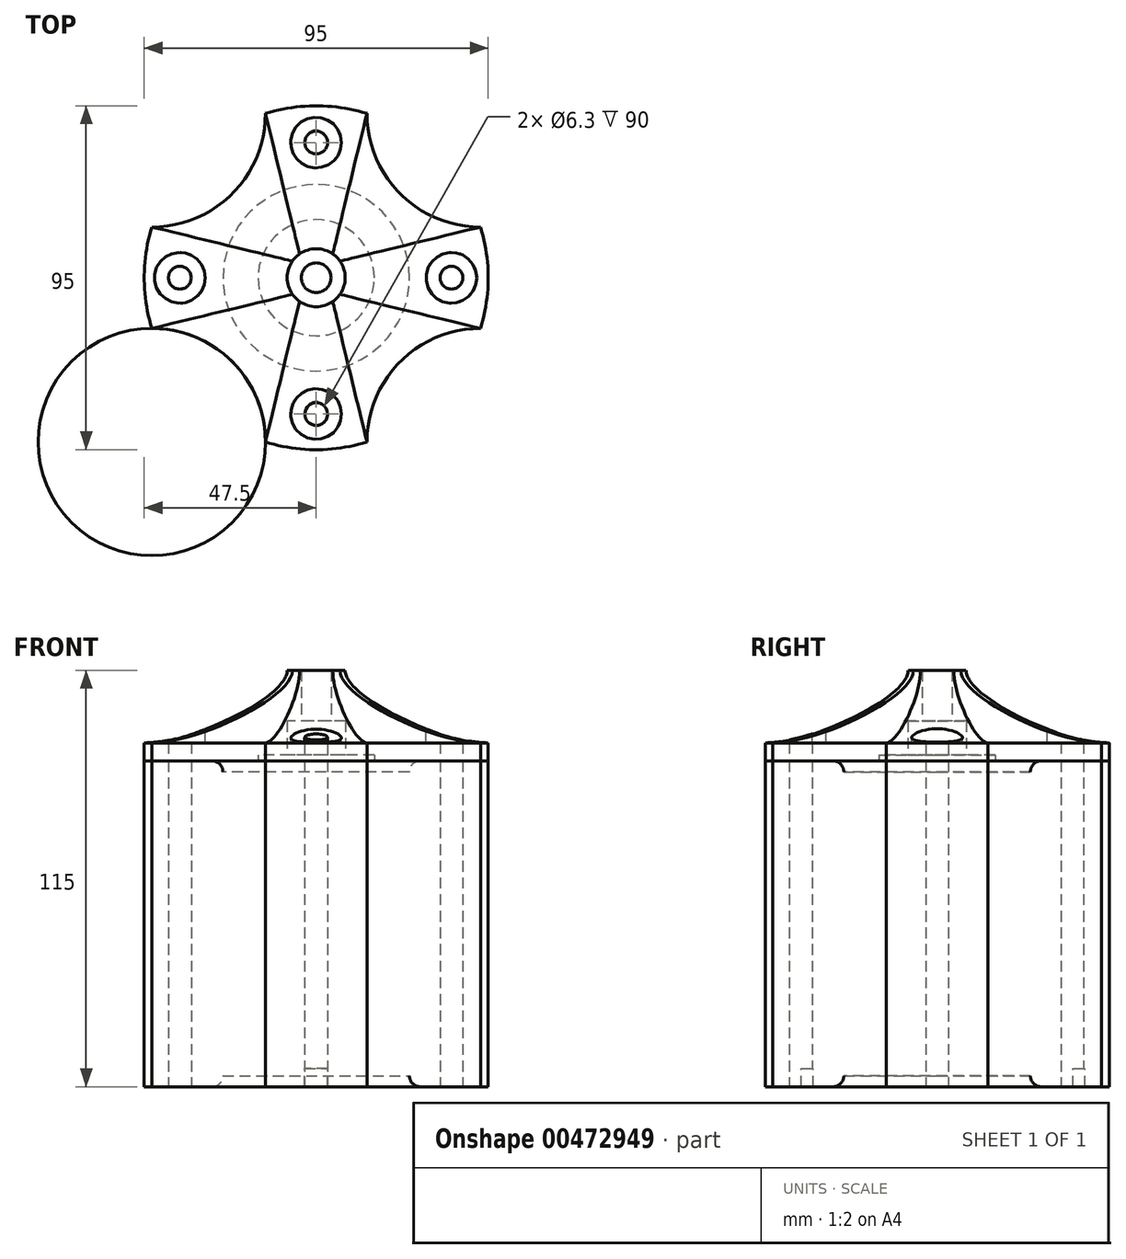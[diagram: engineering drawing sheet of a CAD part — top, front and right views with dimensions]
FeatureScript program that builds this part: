
annotation { "Feature Type Name" : "Feature", "Feature Type Description" : "" }
export const myFeature = defineFeature(function(context is Context, id is Id, definition is map)
    precondition{}
    {
        {
            var Q0;
            Q0=qCreatedBy(makeId("Top.planeOp"),FACE);
            var sketch = newSketch(context, id + "F0", { "sketchPlane" : qUnion([Q0])});
            skArc(sketch, "E0", {"start": v(14, 45.39) * mm, "mid": v(0, 47.5) * mm, "end": v(-14, 45.39) * mm});
            skLineSegment(sketch, "E1", {"start": v(0, 0) * mm, "end": v(47.5, 0) * mm, "construction": true});
            skLineSegment(sketch, "E2", {"start": v(0, 0) * mm, "end": v(-47.5, 0) * mm, "construction": true});
            skLineSegment(sketch, "E3", {"start": v(0, 0) * mm, "end": v(0, 47.5) * mm, "construction": true});
            skLineSegment(sketch, "E4", {"start": v(0, 0) * mm, "end": v(0, -47.5) * mm});
            skCircle(sketch, "E5", {"center": v(37.35, 0) * mm, "radius": 3.15 * mm});
            skCircle(sketch, "E6", {"center": v(-37.65, 0) * mm, "radius": 3.15 * mm});
            skCircle(sketch, "E7", {"center": v(0, 37.35) * mm, "radius": 3.15 * mm});
            skCircle(sketch, "E8", {"center": v(0, -37.65) * mm, "radius": 3.15 * mm});
            skLineSegment(sketch, "E9", {"start": v(14, -45.39) * mm, "end": v(14, 45.39) * mm, "construction": true});
            skLineSegment(sketch, "E10", {"start": v(-14, -45.39) * mm, "end": v(-14, 45.39) * mm, "construction": true});
            skLineSegment(sketch, "E11", {"start": v(-45.39, 14) * mm, "end": v(-14, 14) * mm, "construction": true});
            skLineSegment(sketch, "E12", {"start": v(-45.39, -14) * mm, "end": v(-14, -14) * mm});
            skArc(sketch, "E13.trimOffspring", {"start": v(-45.39, 14) * mm, "mid": v(-47.5, 0) * mm, "end": v(-45.39, -14) * mm});
            skArc(sketch, "E14.trimOffspring", {"start": v(-14, -45.39) * mm, "mid": v(0, -47.5) * mm, "end": v(14, -45.39) * mm});
            skArc(sketch, "E15.trimOffspring", {"start": v(45.39, -14) * mm, "mid": v(47.5, 0) * mm, "end": v(45.39, 14) * mm});
            skArc(sketch, "E16", {"start": v(-45.39, 14) * mm, "mid": v(-23.2, 23.2) * mm, "end": v(-14, 45.39) * mm});
            skLineSegment(sketch, "E17.top", {"start": v(14, 14) * mm, "end": v(45.39, 14) * mm, "construction": true});
            skLineSegment(sketch, "E17.left", {"start": v(14, 45.39) * mm, "end": v(14, 14) * mm, "construction": true});
            skLineSegment(sketch, "E18.top", {"start": v(14, -14) * mm, "end": v(45.39, -14) * mm, "construction": true});
            skLineSegment(sketch, "E18.left", {"start": v(14, -45.39) * mm, "end": v(14, -14) * mm, "construction": true});
            skLineSegment(sketch, "E19.top", {"start": v(-14, -14) * mm, "end": v(-45.39, -14) * mm, "construction": true});
            skLineSegment(sketch, "E19.left", {"start": v(-14, -45.39) * mm, "end": v(-14, -14) * mm, "construction": true});
            skArc(sketch, "E20", {"start": v(-14, -45.39) * mm, "mid": v(-23.2, -23.2) * mm, "end": v(-45.39, -14) * mm});
            skArc(sketch, "E21", {"start": v(45.39, -14) * mm, "mid": v(23.2, -23.2) * mm, "end": v(14, -45.39) * mm});
            skArc(sketch, "E22", {"start": v(14, 45.39) * mm, "mid": v(23.2, 23.2) * mm, "end": v(45.39, 14) * mm});
            skLineSegment(sketch, "E23.trimOffspring", {"start": v(14, 14) * mm, "end": v(45.39, 14) * mm});
            skLineSegment(sketch, "E24.trimOffspring", {"start": v(14, -14) * mm, "end": v(45.39, -14) * mm});
            skCircle(sketch, "E25", {"center": v(0, 0) * mm, "radius": 25.75 * mm});
            skSolve(sketch);
        }
        {
            var Q0;
            Q0=makeQuery(id+"F0.imprint","IMPRINT",FACE,{"disambiguationData":[TD([[makeQuery(id+"F0.imprint","IMPRINT",EDGE,{"derivedFrom":sQuery(id+"F0.wireOp",EDGE,"E0")}),1.0]])]});
            var Q1;
            {var subQ0=sQuery(id+"F0.wireOp",EDGE,"E20");Q1=makeQuery(id+"F0.imprint","IMPRINT",FACE,{"disambiguationData":[TD([[makeQuery(id+"F0.imprint","IMPRINT",EDGE,{"derivedFrom":subQ0}),-1.0]])]});}
            var Q2;
            {var subQ3=sQuery(id+"F0.wireOp",EDGE,"E21");Q2=makeQuery(id+"F0.imprint","IMPRINT",FACE,{"disambiguationData":[TD([[makeQuery(id+"F0.imprint","IMPRINT",EDGE,{"derivedFrom":subQ3}),-1.0]])]});}
            var Q3;
            Q3=makeQuery(id+"F0.imprint","IMPRINT",FACE,{"disambiguationData":[TD([[makeQuery(id+"F0.imprint","IMPRINT",EDGE,{"derivedFrom":sQuery(id+"F0.wireOp",EDGE,"E5")}),-1.0]])]});
            var Q4;
            {var subQ0=sQuery(id+"F0.wireOp",EDGE,"E25");var subQ1=makeQuery(id+"F0.imprint","INTERSECT",VERTEX,{"derivedFrom":[sQuery(id+"F0.wireOp",EDGE,"E12"),subQ0]});Q4=makeQuery(id+"F0.imprint","IMPRINT",FACE,{"disambiguationData":[TD([[makeQuery(id+"F0.imprint","IMPRINT",EDGE,{"disambiguationData":[TD([[subQ1,1.0]])],"derivedFrom":subQ0}),1.0]])]});}
            extrude(context, id + "F1", {"entities" : qUnion([Q0, Q1, Q2, Q3, Q4]), "depth" : 80 * mm, "symmetric" : true});
        }
        {
            var Q0;
            Q0=makeQuery(id+"F1.opExtrude","CAP_FACE",FACE,{"disambiguationData":[OSD([sQuery(id+"F0.wireOp",EDGE,"E0"),sQuery(id+"F0.wireOp",EDGE,"E5"),sQuery(id+"F0.wireOp",EDGE,"E6"),sQuery(id+"F0.wireOp",EDGE,"E7"),sQuery(id+"F0.wireOp",EDGE,"E8"),sQuery(id+"F0.wireOp",EDGE,"E13.trimOffspring"),sQuery(id+"F0.wireOp",EDGE,"E14.trimOffspring"),sQuery(id+"F0.wireOp",EDGE,"E15.trimOffspring"),sQuery(id+"F0.wireOp",EDGE,"E16"),sQuery(id+"F0.wireOp",EDGE,"E20"),sQuery(id+"F0.wireOp",EDGE,"E21"),sQuery(id+"F0.wireOp",EDGE,"E22")])],"isStart":false});
            cPlane(context, id + "F2", {"entities" : qUnion([Q0]), "cplaneType" : CPlaneType.OFFSET, "offset" : 5 * mm, "width" : 150 * mm, "height" : 150 * mm});
        }
        {
            var Q0;
            Q0=qCreatedBy(id+"F2.planeOp",FACE);
            var sketch = newSketch(context, id + "F3", { "sketchPlane" : qUnion([Q0])});
            skArc(sketch, "E26", {"start": v(14, 45.39) * mm, "mid": v(0, 47.5) * mm, "end": v(-14, 45.39) * mm});
            skLineSegment(sketch, "E27", {"start": v(0, 0) * mm, "end": v(47.5, 0) * mm, "construction": true});
            skLineSegment(sketch, "E28", {"start": v(0, 0) * mm, "end": v(-47.5, 0) * mm, "construction": true});
            skLineSegment(sketch, "E29", {"start": v(0, 0) * mm, "end": v(0, 47.5) * mm, "construction": true});
            skLineSegment(sketch, "E30", {"start": v(0, 0) * mm, "end": v(0, -47.5) * mm});
            skCircle(sketch, "E31", {"center": v(37.35, 0) * mm, "radius": 3.15 * mm});
            skCircle(sketch, "E32", {"center": v(-37.65, 0) * mm, "radius": 3.15 * mm});
            skCircle(sketch, "E33", {"center": v(0, 37.35) * mm, "radius": 3.15 * mm});
            skCircle(sketch, "E34", {"center": v(0, -37.65) * mm, "radius": 3.15 * mm});
            skLineSegment(sketch, "E35", {"start": v(14, -45.39) * mm, "end": v(14, 45.39) * mm, "construction": true});
            skLineSegment(sketch, "E36", {"start": v(-14, -45.39) * mm, "end": v(-14, 45.39) * mm, "construction": true});
            skLineSegment(sketch, "E37", {"start": v(-45.39, 14) * mm, "end": v(-14, 14) * mm, "construction": true});
            skLineSegment(sketch, "E38", {"start": v(-45.39, -14) * mm, "end": v(-14, -14) * mm});
            skArc(sketch, "E39.trimOffspring", {"start": v(-45.39, 14) * mm, "mid": v(-47.5, 0) * mm, "end": v(-45.39, -14) * mm});
            skArc(sketch, "E40.trimOffspring", {"start": v(-14, -45.39) * mm, "mid": v(0, -47.5) * mm, "end": v(14, -45.39) * mm});
            skArc(sketch, "E41.trimOffspring", {"start": v(45.39, -14) * mm, "mid": v(47.5, 0) * mm, "end": v(45.39, 14) * mm});
            skArc(sketch, "E42", {"start": v(-45.39, 14) * mm, "mid": v(-23.2, 23.2) * mm, "end": v(-14, 45.39) * mm});
            skLineSegment(sketch, "E43.top", {"start": v(14, 14) * mm, "end": v(45.39, 14) * mm, "construction": true});
            skLineSegment(sketch, "E43.left", {"start": v(14, 45.39) * mm, "end": v(14, 14) * mm, "construction": true});
            skLineSegment(sketch, "E44.top", {"start": v(14, -14) * mm, "end": v(45.39, -14) * mm, "construction": true});
            skLineSegment(sketch, "E44.left", {"start": v(14, -45.39) * mm, "end": v(14, -14) * mm, "construction": true});
            skLineSegment(sketch, "E45.top", {"start": v(-14, -14) * mm, "end": v(-45.39, -14) * mm, "construction": true});
            skLineSegment(sketch, "E45.left", {"start": v(-14, -45.39) * mm, "end": v(-14, -14) * mm, "construction": true});
            skArc(sketch, "E46", {"start": v(-14, -45.39) * mm, "mid": v(-23.2, -23.2) * mm, "end": v(-45.39, -14) * mm});
            skArc(sketch, "E47", {"start": v(45.39, -14) * mm, "mid": v(23.2, -23.2) * mm, "end": v(14, -45.39) * mm});
            skArc(sketch, "E48", {"start": v(14, 45.39) * mm, "mid": v(23.2, 23.2) * mm, "end": v(45.39, 14) * mm});
            skLineSegment(sketch, "E49.trimOffspring", {"start": v(14, 14) * mm, "end": v(45.39, 14) * mm});
            skLineSegment(sketch, "E50.trimOffspring", {"start": v(14, -14) * mm, "end": v(45.39, -14) * mm});
            skCircle(sketch, "E51", {"center": v(0, 0) * mm, "radius": 25.75 * mm});
            skSolve(sketch);
        }
        {
            var Q0;
            Q0=makeQuery(id+"F3.imprint","IMPRINT",FACE,{"disambiguationData":[TD([[makeQuery(id+"F3.imprint","IMPRINT",EDGE,{"derivedFrom":sQuery(id+"F3.wireOp",EDGE,"E26")}),1.0]])]});
            var Q1;
            Q1=makeQuery(id+"F3.imprint","IMPRINT",FACE,{"disambiguationData":[TD([[makeQuery(id+"F3.imprint","IMPRINT",EDGE,{"derivedFrom":sQuery(id+"F3.wireOp",EDGE,"E31")}),-1.0]])]});
            var Q2;
            {var subQ3=sQuery(id+"F3.wireOp",EDGE,"E47");Q2=makeQuery(id+"F3.imprint","IMPRINT",FACE,{"disambiguationData":[TD([[makeQuery(id+"F3.imprint","IMPRINT",EDGE,{"derivedFrom":subQ3}),-1.0]])]});}
            var Q3;
            {var subQ0=sQuery(id+"F3.wireOp",EDGE,"E46");Q3=makeQuery(id+"F3.imprint","IMPRINT",FACE,{"disambiguationData":[TD([[makeQuery(id+"F3.imprint","IMPRINT",EDGE,{"derivedFrom":subQ0}),-1.0]])]});}
            extrude(context, id + "F4", {"entities" : qUnion([Q0, Q1, Q2, Q3]), "operationType" : NewBodyOperationType.ADD, "oppositeDirection" : true, "depth" : 5 * mm});
        }
        {
            var Q0;
            Q0=makeQuery(id+"F1.opExtrude","CAP_FACE",FACE,{"disambiguationData":[OSD([sQuery(id+"F0.wireOp",EDGE,"E0"),sQuery(id+"F0.wireOp",EDGE,"E5"),sQuery(id+"F0.wireOp",EDGE,"E6"),sQuery(id+"F0.wireOp",EDGE,"E7"),sQuery(id+"F0.wireOp",EDGE,"E8"),sQuery(id+"F0.wireOp",EDGE,"E13.trimOffspring"),sQuery(id+"F0.wireOp",EDGE,"E14.trimOffspring"),sQuery(id+"F0.wireOp",EDGE,"E15.trimOffspring"),sQuery(id+"F0.wireOp",EDGE,"E16"),sQuery(id+"F0.wireOp",EDGE,"E20"),sQuery(id+"F0.wireOp",EDGE,"E21"),sQuery(id+"F0.wireOp",EDGE,"E22")])],"isStart":false});
            extrude(context, id + "F5", {"entities" : qUnion([Q0]), "operationType" : NewBodyOperationType.ADD, "depth" : 2 * mm});
        }
        {
            var Q0;
            Q0=makeQuery(id+"F1.opExtrude","CAP_FACE",FACE,{"disambiguationData":[OSD([sQuery(id+"F0.wireOp",EDGE,"E0"),sQuery(id+"F0.wireOp",EDGE,"E5"),sQuery(id+"F0.wireOp",EDGE,"E6"),sQuery(id+"F0.wireOp",EDGE,"E7"),sQuery(id+"F0.wireOp",EDGE,"E8"),sQuery(id+"F0.wireOp",EDGE,"E13.trimOffspring"),sQuery(id+"F0.wireOp",EDGE,"E14.trimOffspring"),sQuery(id+"F0.wireOp",EDGE,"E15.trimOffspring"),sQuery(id+"F0.wireOp",EDGE,"E16"),sQuery(id+"F0.wireOp",EDGE,"E20"),sQuery(id+"F0.wireOp",EDGE,"E21"),sQuery(id+"F0.wireOp",EDGE,"E22")])],"isStart":true});
            var sketch = newSketch(context, id + "F6", { "sketchPlane" : qUnion([Q0])});
            skArc(sketch, "E52", {"start": v(14, 45.39) * mm, "mid": v(0, 47.5) * mm, "end": v(-14, 45.39) * mm});
            skLineSegment(sketch, "E53", {"start": v(0, 0) * mm, "end": v(47.5, 0) * mm, "construction": true});
            skLineSegment(sketch, "E54", {"start": v(0, 0) * mm, "end": v(-47.5, 0) * mm, "construction": true});
            skLineSegment(sketch, "E55", {"start": v(0, 0) * mm, "end": v(0, 47.5) * mm, "construction": true});
            skLineSegment(sketch, "E56", {"start": v(0, 0) * mm, "end": v(0, -47.5) * mm});
            skCircle(sketch, "E57", {"center": v(37.35, 0) * mm, "radius": 3.15 * mm});
            skCircle(sketch, "E58", {"center": v(-37.65, 0) * mm, "radius": 3.15 * mm});
            skCircle(sketch, "E59", {"center": v(0, 37.35) * mm, "radius": 3.15 * mm});
            skCircle(sketch, "E60", {"center": v(0, -37.65) * mm, "radius": 3.15 * mm});
            skLineSegment(sketch, "E61", {"start": v(14, -45.39) * mm, "end": v(14, 45.39) * mm, "construction": true});
            skLineSegment(sketch, "E62", {"start": v(-14, -45.39) * mm, "end": v(-14, 45.39) * mm, "construction": true});
            skLineSegment(sketch, "E63", {"start": v(-45.39, 14) * mm, "end": v(-14, 14) * mm, "construction": true});
            skLineSegment(sketch, "E64", {"start": v(-45.39, -14) * mm, "end": v(-14, -14) * mm});
            skArc(sketch, "E65.trimOffspring", {"start": v(-45.39, 14) * mm, "mid": v(-47.5, 0) * mm, "end": v(-45.39, -14) * mm});
            skArc(sketch, "E66.trimOffspring", {"start": v(-14, -45.39) * mm, "mid": v(0, -47.5) * mm, "end": v(14, -45.39) * mm});
            skArc(sketch, "E67.trimOffspring", {"start": v(45.39, -14) * mm, "mid": v(47.5, 0) * mm, "end": v(45.39, 14) * mm});
            skArc(sketch, "E68", {"start": v(-45.39, 14) * mm, "mid": v(-23.2, 23.2) * mm, "end": v(-14, 45.39) * mm});
            skLineSegment(sketch, "E69.top", {"start": v(14, 14) * mm, "end": v(45.39, 14) * mm, "construction": true});
            skLineSegment(sketch, "E69.left", {"start": v(14, 45.39) * mm, "end": v(14, 14) * mm, "construction": true});
            skLineSegment(sketch, "E70.top", {"start": v(14, -14) * mm, "end": v(45.39, -14) * mm, "construction": true});
            skLineSegment(sketch, "E70.left", {"start": v(14, -45.39) * mm, "end": v(14, -14) * mm, "construction": true});
            skLineSegment(sketch, "E71.top", {"start": v(-14, -14) * mm, "end": v(-45.39, -14) * mm, "construction": true});
            skLineSegment(sketch, "E71.left", {"start": v(-14, -45.39) * mm, "end": v(-14, -14) * mm, "construction": true});
            skArc(sketch, "E72", {"start": v(-14, -45.39) * mm, "mid": v(-23.2, -23.2) * mm, "end": v(-45.39, -14) * mm});
            skArc(sketch, "E73", {"start": v(45.39, -14) * mm, "mid": v(23.2, -23.2) * mm, "end": v(14, -45.39) * mm});
            skArc(sketch, "E74", {"start": v(14, 45.39) * mm, "mid": v(23.2, 23.2) * mm, "end": v(45.39, 14) * mm});
            skLineSegment(sketch, "E75.trimOffspring", {"start": v(14, 14) * mm, "end": v(45.39, 14) * mm});
            skLineSegment(sketch, "E76.trimOffspring", {"start": v(14, -14) * mm, "end": v(45.39, -14) * mm});
            skCircle(sketch, "E77", {"center": v(0, 0) * mm, "radius": 25.75 * mm});
            skSolve(sketch);
        }
        {
            var Q0;
            Q0=makeQuery(id+"F6.imprint","IMPRINT",FACE,{"disambiguationData":[TD([[makeQuery(id+"F6.imprint","IMPRINT",EDGE,{"derivedFrom":sQuery(id+"F6.wireOp",EDGE,"E52")}),-1.0]])]});
            var Q1;
            {var subQ0=sQuery(id+"F6.wireOp",EDGE,"E72");Q1=makeQuery(id+"F6.imprint","IMPRINT",FACE,{"disambiguationData":[TD([[makeQuery(id+"F6.imprint","IMPRINT",EDGE,{"derivedFrom":subQ0}),1.0]])]});}
            var Q2;
            {var subQ6=sQuery(id+"F6.wireOp",EDGE,"E73");Q2=makeQuery(id+"F6.imprint","IMPRINT",FACE,{"disambiguationData":[TD([[makeQuery(id+"F6.imprint","IMPRINT",EDGE,{"derivedFrom":subQ6}),1.0]])]});}
            var Q3;
            Q3=makeQuery(id+"F6.imprint","IMPRINT",FACE,{"disambiguationData":[TD([[makeQuery(id+"F6.imprint","IMPRINT",EDGE,{"derivedFrom":sQuery(id+"F6.wireOp",EDGE,"E57")}),1.0]])]});
            extrude(context, id + "F7", {"entities" : qUnion([Q0, Q1, Q2, Q3]), "operationType" : NewBodyOperationType.ADD, "depth" : 5 * mm});
        }
        {
            var Q0;
            Q0=makeQuery(id+"F7.opExtrude","CAP_EDGE",EDGE,{"disambiguationData":[OSD([sQuery(id+"F6.wireOp",EDGE,"E77")])],"isStart":false});
            var Q1;
            Q1=makeQuery(id+"F4.opExtrude","CAP_EDGE",EDGE,{"disambiguationData":[OSD([sQuery(id+"F3.wireOp",EDGE,"E51")])],"isStart":true});
            fillet(context, id + "F8", {"entities" : qUnion([Q0, Q1]), "radius" : 3 * mm, "tangentPropagation" : true, "allowEdgeOverflow" : false});
        }
        {
            var Q0;
            {var subQ0=sQuery(id+"F6.wireOp",EDGE,"E77");var subQ1=makeQuery(id+"F6.imprint","INTERSECT",VERTEX,{"derivedFrom":[sQuery(id+"F6.wireOp",EDGE,"E64"),subQ0]});Q0=makeQuery(id+"F6.imprint","IMPRINT",FACE,{"disambiguationData":[TD([[makeQuery(id+"F6.imprint","IMPRINT",EDGE,{"disambiguationData":[TD([[subQ1,1.0]])],"derivedFrom":subQ0}),1.0]])]});}
            extrude(context, id + "F9", {"entities" : qUnion([Q0]), "operationType" : NewBodyOperationType.ADD, "depth" : 2 * mm});
        }
        {
            var Q0;
            Q0=makeQuery(id+"F3.imprint","IMPRINT",FACE,{"disambiguationData":[TD([[makeQuery(id+"F3.imprint","IMPRINT",EDGE,{"derivedFrom":sQuery(id+"F3.wireOp",EDGE,"E31")}),-1.0]])]});
            var sketch = newSketch(context, id + "F10", { "sketchPlane" : qUnion([Q0])});
            skArc(sketch, "E78", {"start": v(14, 45.39) * mm, "mid": v(0, 47.5) * mm, "end": v(-14, 45.39) * mm});
            skLineSegment(sketch, "E79", {"start": v(0, 0) * mm, "end": v(47.5, 0) * mm, "construction": true});
            skLineSegment(sketch, "E80", {"start": v(0, 0) * mm, "end": v(-47.5, 0) * mm, "construction": true});
            skLineSegment(sketch, "E81", {"start": v(0, 0) * mm, "end": v(0, 47.5) * mm, "construction": true});
            skLineSegment(sketch, "E82", {"start": v(0, 0) * mm, "end": v(0, -47.5) * mm});
            skCircle(sketch, "E83", {"center": v(37.35, 0) * mm, "radius": 3.15 * mm});
            skCircle(sketch, "E84", {"center": v(-37.65, 0) * mm, "radius": 3.15 * mm});
            skCircle(sketch, "E85", {"center": v(0, 37.35) * mm, "radius": 3.15 * mm});
            skCircle(sketch, "E86", {"center": v(0, -37.65) * mm, "radius": 3.15 * mm});
            skLineSegment(sketch, "E87", {"start": v(14, -45.39) * mm, "end": v(14, 45.39) * mm, "construction": true});
            skLineSegment(sketch, "E88", {"start": v(-14, -45.39) * mm, "end": v(-14, 45.39) * mm, "construction": true});
            skLineSegment(sketch, "E89", {"start": v(-45.39, 14) * mm, "end": v(-14, 14) * mm, "construction": true});
            skLineSegment(sketch, "E90", {"start": v(-45.39, -14) * mm, "end": v(-14, -14) * mm});
            skArc(sketch, "E91.trimOffspring", {"start": v(-45.39, 14) * mm, "mid": v(-47.5, 0) * mm, "end": v(-45.39, -14) * mm});
            skArc(sketch, "E92.trimOffspring", {"start": v(-14, -45.39) * mm, "mid": v(0, -47.5) * mm, "end": v(14, -45.39) * mm});
            skArc(sketch, "E93.trimOffspring", {"start": v(45.39, -14) * mm, "mid": v(47.5, 0) * mm, "end": v(45.39, 14) * mm});
            skArc(sketch, "E94", {"start": v(-45.39, 14) * mm, "mid": v(-23.2, 23.2) * mm, "end": v(-14, 45.39) * mm});
            skLineSegment(sketch, "E95.top", {"start": v(14, 14) * mm, "end": v(45.39, 14) * mm, "construction": true});
            skLineSegment(sketch, "E95.left", {"start": v(14, 45.39) * mm, "end": v(14, 14) * mm, "construction": true});
            skLineSegment(sketch, "E96.top", {"start": v(14, -14) * mm, "end": v(45.39, -14) * mm, "construction": true});
            skLineSegment(sketch, "E96.left", {"start": v(14, -45.39) * mm, "end": v(14, -14) * mm, "construction": true});
            skLineSegment(sketch, "E97.top", {"start": v(-14, -14) * mm, "end": v(-45.39, -14) * mm, "construction": true});
            skLineSegment(sketch, "E97.left", {"start": v(-14, -45.39) * mm, "end": v(-14, -14) * mm, "construction": true});
            skArc(sketch, "E98", {"start": v(-14, -45.39) * mm, "mid": v(-23.2, -23.2) * mm, "end": v(-45.39, -14) * mm});
            skArc(sketch, "E99", {"start": v(45.39, -14) * mm, "mid": v(23.2, -23.2) * mm, "end": v(14, -45.39) * mm});
            skArc(sketch, "E100", {"start": v(14, 45.39) * mm, "mid": v(23.2, 23.2) * mm, "end": v(45.39, 14) * mm});
            skLineSegment(sketch, "E101.trimOffspring", {"start": v(14, 14) * mm, "end": v(45.39, 14) * mm});
            skLineSegment(sketch, "E102.trimOffspring", {"start": v(14, -14) * mm, "end": v(45.39, -14) * mm});
            skCircle(sketch, "E103", {"center": v(0, 0) * mm, "radius": 16.05 * mm});
            skCircle(sketch, "E104", {"center": v(0, 0) * mm, "radius": 8.05 * mm});
            skCircle(sketch, "E105", {"center": v(0, 0) * mm, "radius": 4.1 * mm});
            skSolve(sketch);
        }
        {
            var Q0;
            Q0 = qSketchRegion(id + "F10", true);
            var Q1;
            Q1=makeQuery(id+"F10.imprint","IMPRINT",FACE,{"disambiguationData":[TD([[makeQuery(id+"F10.imprint","IMPRINT",EDGE,{"derivedFrom":sQuery(id+"F10.wireOp",EDGE,"E103")}),1.0]])]});
            var Q2;
            Q2=makeQuery(id+"F10.imprint","IMPRINT",FACE,{"disambiguationData":[TD([[makeQuery(id+"F10.imprint","IMPRINT",EDGE,{"derivedFrom":sQuery(id+"F10.wireOp",EDGE,"E104")}),1.0]])]});
            var Q3;
            Q3=makeQuery(id+"F10.imprint","IMPRINT",FACE,{"disambiguationData":[TD([[makeQuery(id+"F10.imprint","IMPRINT",EDGE,{"derivedFrom":sQuery(id+"F10.wireOp",EDGE,"E105")}),1.0]])]});
            extrude(context, id + "F11", {"entities" : qUnion([Q0, Q1, Q2, Q3]), "depth" : 5 * mm, "offsetDistance" : 25 * mm});
        }
        {
            var Q0;
            Q0=makeQuery(id+"F11.opExtrude","CAP_FACE",FACE,{"disambiguationData":[OSD([sQuery(id+"F10.wireOp",EDGE,"E78"),sQuery(id+"F10.wireOp",EDGE,"E83"),sQuery(id+"F10.wireOp",EDGE,"E84"),sQuery(id+"F10.wireOp",EDGE,"E85"),sQuery(id+"F10.wireOp",EDGE,"E86"),sQuery(id+"F10.wireOp",EDGE,"E91.trimOffspring"),sQuery(id+"F10.wireOp",EDGE,"E92.trimOffspring"),sQuery(id+"F10.wireOp",EDGE,"E93.trimOffspring"),sQuery(id+"F10.wireOp",EDGE,"E94"),sQuery(id+"F10.wireOp",EDGE,"E98"),sQuery(id+"F10.wireOp",EDGE,"E99"),sQuery(id+"F10.wireOp",EDGE,"E100")])],"isStart":false});
            cPlane(context, id + "F12", {"entities" : qUnion([Q0]), "cplaneType" : CPlaneType.OFFSET, "offset" : 20 * mm, "width" : 150 * mm, "height" : 150 * mm});
        }
        {
            var Q0;
            Q0=makeQuery(id+"F11.opExtrude","CAP_FACE",FACE,{"disambiguationData":[OSD([sQuery(id+"F10.wireOp",EDGE,"E78"),sQuery(id+"F10.wireOp",EDGE,"E83"),sQuery(id+"F10.wireOp",EDGE,"E84"),sQuery(id+"F10.wireOp",EDGE,"E85"),sQuery(id+"F10.wireOp",EDGE,"E86"),sQuery(id+"F10.wireOp",EDGE,"E91.trimOffspring"),sQuery(id+"F10.wireOp",EDGE,"E92.trimOffspring"),sQuery(id+"F10.wireOp",EDGE,"E93.trimOffspring"),sQuery(id+"F10.wireOp",EDGE,"E94"),sQuery(id+"F10.wireOp",EDGE,"E98"),sQuery(id+"F10.wireOp",EDGE,"E99"),sQuery(id+"F10.wireOp",EDGE,"E100")])],"isStart":false});
            var sketch = newSketch(context, id + "F13", { "sketchPlane" : qUnion([Q0])});
            skArc(sketch, "E106", {"start": v(14, 45.39) * mm, "mid": v(0, 47.5) * mm, "end": v(-14, 45.39) * mm});
            skLineSegment(sketch, "E107", {"start": v(0, 0) * mm, "end": v(47.5, 0) * mm, "construction": true});
            skLineSegment(sketch, "E108", {"start": v(0, 0) * mm, "end": v(-47.5, 0) * mm, "construction": true});
            skLineSegment(sketch, "E109", {"start": v(0, 0) * mm, "end": v(0, 47.5) * mm, "construction": true});
            skLineSegment(sketch, "E110", {"start": v(0, 0) * mm, "end": v(0, -47.5) * mm});
            skLineSegment(sketch, "E111", {"start": v(14, -45.39) * mm, "end": v(14, 45.39) * mm, "construction": true});
            skLineSegment(sketch, "E112", {"start": v(-14, -45.39) * mm, "end": v(-14, 45.39) * mm, "construction": true});
            skLineSegment(sketch, "E113", {"start": v(-45.39, 14) * mm, "end": v(-14, 14) * mm, "construction": true});
            skLineSegment(sketch, "E114", {"start": v(-45.39, -14) * mm, "end": v(-14, -14) * mm});
            skArc(sketch, "E115.trimOffspring", {"start": v(-45.39, 14) * mm, "mid": v(-47.5, 0) * mm, "end": v(-45.39, -14) * mm});
            skArc(sketch, "E116.trimOffspring", {"start": v(-14, -45.39) * mm, "mid": v(0, -47.5) * mm, "end": v(14, -45.39) * mm});
            skArc(sketch, "E117.trimOffspring", {"start": v(45.39, -14) * mm, "mid": v(47.5, 0) * mm, "end": v(45.39, 14) * mm});
            skArc(sketch, "E118", {"start": v(-45.39, 14) * mm, "mid": v(-23.2, 23.2) * mm, "end": v(-14, 45.39) * mm});
            skLineSegment(sketch, "E119.top", {"start": v(14, 14) * mm, "end": v(45.39, 14) * mm, "construction": true});
            skLineSegment(sketch, "E119.left", {"start": v(14, 45.39) * mm, "end": v(14, 14) * mm, "construction": true});
            skLineSegment(sketch, "E120.top", {"start": v(14, -14) * mm, "end": v(45.39, -14) * mm, "construction": true});
            skLineSegment(sketch, "E120.left", {"start": v(14, -45.39) * mm, "end": v(14, -14) * mm, "construction": true});
            skLineSegment(sketch, "E121.top", {"start": v(-14, -14) * mm, "end": v(-45.39, -14) * mm, "construction": true});
            skLineSegment(sketch, "E121.left", {"start": v(-14, -45.39) * mm, "end": v(-14, -14) * mm, "construction": true});
            skArc(sketch, "E122", {"start": v(-14, -45.39) * mm, "mid": v(-23.2, -23.2) * mm, "end": v(-45.39, -14) * mm});
            skArc(sketch, "E123", {"start": v(45.39, -14) * mm, "mid": v(23.2, -23.2) * mm, "end": v(14, -45.39) * mm});
            skArc(sketch, "E124", {"start": v(14, 45.39) * mm, "mid": v(23.2, 23.2) * mm, "end": v(45.39, 14) * mm});
            skLineSegment(sketch, "E125.trimOffspring", {"start": v(14, 14) * mm, "end": v(45.39, 14) * mm});
            skLineSegment(sketch, "E126.trimOffspring", {"start": v(14, -14) * mm, "end": v(45.39, -14) * mm});
            skSolve(sketch);
        }
        {
            var Q0;
            Q0=qCreatedBy(id+"F12.planeOp",FACE);
            var sketch = newSketch(context, id + "F14", { "sketchPlane" : qUnion([Q0])});
            skArc(sketch, "E127", {"start": v(-4.59, -6.55) * mm, "mid": v(0, -8) * mm, "end": v(4.59, -6.55) * mm});
            skLineSegment(sketch, "E128", {"start": v(0, -8) * mm, "end": v(0, 8) * mm, "construction": true});
            skLineSegment(sketch, "E129", {"start": v(-8, 0) * mm, "end": v(8, 0) * mm, "construction": true});
            skLineSegment(sketch, "E130", {"start": v(0, 0) * mm, "end": v(-4.59, -6.55) * mm});
            skLineSegment(sketch, "E131", {"start": v(0, 0) * mm, "end": v(4.59, -6.55) * mm});
            skLineSegment(sketch, "E132", {"start": v(0, 0) * mm, "end": v(6.55, -4.59) * mm});
            skLineSegment(sketch, "E133", {"start": v(0, 0) * mm, "end": v(6.55, 4.59) * mm});
            skLineSegment(sketch, "E134", {"start": v(0, 0) * mm, "end": v(4.59, 6.55) * mm});
            skLineSegment(sketch, "E135", {"start": v(0, 0) * mm, "end": v(-4.59, 6.55) * mm});
            skLineSegment(sketch, "E136", {"start": v(0, 0) * mm, "end": v(-6.55, -4.59) * mm});
            skArc(sketch, "E137.trimOffspring", {"start": v(6.55, -4.59) * mm, "mid": v(8, 0) * mm, "end": v(6.55, 4.59) * mm});
            skCircle(sketch, "E138", {"center": v(0, 0) * mm, "radius": 8 * mm});
            skLineSegment(sketch, "E139", {"start": v(0, 0) * mm, "end": v(-6.55, 4.59) * mm});
            skLineSegment(sketch, "E140", {"start": v(0, 0) * mm, "end": v(0, -47.5) * mm, "construction": true});
            skSolve(sketch);
        }
        {
            var Q0;
            Q0 = qSketchRegion(id + "F13", true);
            var Q1;
            Q1 = qSketchRegion(id + "F14", true);
            var Q2;
            Q2=sQuery(id+"F13.wireOp",VERTEX,"E112.start");
            var Q3;
            Q3=sQuery(id+"F14.wireOp",VERTEX,"E127.start");
            loft(context, id + "F15", {"operationType" : NewBodyOperationType.ADD, "startCondition" : LoftEndDerivativeType.TANGENT_TO_PROFILE, "startMagnitude" : 1, "endCondition" : LoftEndDerivativeType.NORMAL_TO_PROFILE, "endMagnitude" : 1, "sheetProfilesArray" : [{ "sheetProfileEntities" : qUnion([Q0]) }, { "sheetProfileEntities" : qUnion([Q1]) }], "matchConnections" : true, "connections" : [{ "connectionEntities" : qUnion([Q2, Q3]), "connectionEdgeQueries" : qUnion([]), "connectionEdgeParameters" : [] }]});
        }
        {
            var Q0;
            {var subQ0=sQuery(id+"F14.wireOp",EDGE,"E130");Q0=makeQuery(id+"F14.imprint","IMPRINT",FACE,{"disambiguationData":[TD([[makeQuery(id+"F14.imprint","IMPRINT",EDGE,{"derivedFrom":subQ0}),-1.0]])]});}
            cPlane(context, id + "F16", {"entities" : qUnion([Q0]), "cplaneType" : CPlaneType.OFFSET, "offset" : 5 * mm, "width" : 150 * mm, "height" : 150 * mm});
        }
        {
            var Q0;
            Q0=qCreatedBy(id+"F16.planeOp",FACE);
            var sketch = newSketch(context, id + "F17", { "sketchPlane" : qUnion([Q0])});
            skArc(sketch, "E141", {"start": v(14, 45.39) * mm, "mid": v(0, 47.5) * mm, "end": v(-14, 45.39) * mm});
            skLineSegment(sketch, "E142", {"start": v(0, 0) * mm, "end": v(47.5, 0) * mm, "construction": true});
            skLineSegment(sketch, "E143", {"start": v(0, 0) * mm, "end": v(-47.5, 0) * mm, "construction": true});
            skLineSegment(sketch, "E144", {"start": v(0, 0) * mm, "end": v(0, 47.5) * mm, "construction": true});
            skLineSegment(sketch, "E145", {"start": v(0, 0) * mm, "end": v(0, -47.5) * mm});
            skCircle(sketch, "E146", {"center": v(37.35, 0) * mm, "radius": 3.15 * mm});
            skCircle(sketch, "E147", {"center": v(-37.65, 0) * mm, "radius": 3.15 * mm});
            skCircle(sketch, "E148", {"center": v(0, 37.35) * mm, "radius": 3.15 * mm});
            skCircle(sketch, "E149", {"center": v(0, -37.65) * mm, "radius": 3.15 * mm});
            skLineSegment(sketch, "E150", {"start": v(14, -45.39) * mm, "end": v(14, 45.39) * mm, "construction": true});
            skLineSegment(sketch, "E151", {"start": v(-14, -45.39) * mm, "end": v(-14, 45.39) * mm, "construction": true});
            skLineSegment(sketch, "E152", {"start": v(-45.39, 14) * mm, "end": v(-14, 14) * mm, "construction": true});
            skLineSegment(sketch, "E153", {"start": v(-45.39, -14) * mm, "end": v(-14, -14) * mm});
            skArc(sketch, "E154.trimOffspring", {"start": v(-45.39, 14) * mm, "mid": v(-47.5, 0) * mm, "end": v(-45.39, -14) * mm});
            skArc(sketch, "E155.trimOffspring", {"start": v(-14, -45.39) * mm, "mid": v(0, -47.5) * mm, "end": v(14, -45.39) * mm});
            skArc(sketch, "E156.trimOffspring", {"start": v(45.39, -14) * mm, "mid": v(47.5, 0) * mm, "end": v(45.39, 14) * mm});
            skArc(sketch, "E157", {"start": v(-45.39, 14) * mm, "mid": v(-23.2, 23.2) * mm, "end": v(-14, 45.39) * mm});
            skLineSegment(sketch, "E158.top", {"start": v(14, 14) * mm, "end": v(45.39, 14) * mm, "construction": true});
            skLineSegment(sketch, "E158.left", {"start": v(14, 45.39) * mm, "end": v(14, 14) * mm, "construction": true});
            skLineSegment(sketch, "E159.top", {"start": v(14, -14) * mm, "end": v(45.39, -14) * mm, "construction": true});
            skLineSegment(sketch, "E159.left", {"start": v(14, -45.39) * mm, "end": v(14, -14) * mm, "construction": true});
            skLineSegment(sketch, "E160.top", {"start": v(-14, -14) * mm, "end": v(-45.39, -14) * mm, "construction": true});
            skLineSegment(sketch, "E160.left", {"start": v(-14, -45.39) * mm, "end": v(-14, -14) * mm, "construction": true});
            skArc(sketch, "E161", {"start": v(-14, -45.39) * mm, "mid": v(-23.2, -23.2) * mm, "end": v(-45.39, -14) * mm});
            skArc(sketch, "E162", {"start": v(45.39, -14) * mm, "mid": v(23.2, -23.2) * mm, "end": v(14, -45.39) * mm});
            skArc(sketch, "E163", {"start": v(14, 45.39) * mm, "mid": v(23.2, 23.2) * mm, "end": v(45.39, 14) * mm});
            skLineSegment(sketch, "E164.trimOffspring", {"start": v(14, 14) * mm, "end": v(45.39, 14) * mm});
            skLineSegment(sketch, "E165.trimOffspring", {"start": v(14, -14) * mm, "end": v(45.39, -14) * mm});
            skCircle(sketch, "E166", {"center": v(0, 0) * mm, "radius": 25.75 * mm});
            skCircle(sketch, "E167", {"center": v(-37.65, 0) * mm, "radius": 7 * mm});
            skCircle(sketch, "E168", {"center": v(37.35, 0) * mm, "radius": 7 * mm});
            skCircle(sketch, "E169", {"center": v(0, 37.35) * mm, "radius": 7 * mm});
            skCircle(sketch, "E170", {"center": v(0, -37.65) * mm, "radius": 7 * mm});
            skSolve(sketch);
        }
        {
            var Q0;
            Q0=makeQuery(id+"F17.imprint","IMPRINT",FACE,{"disambiguationData":[TD([[makeQuery(id+"F17.imprint","IMPRINT",EDGE,{"derivedFrom":sQuery(id+"F17.wireOp",EDGE,"E146")}),-1.0]])]});
            var Q1;
            Q1=makeQuery(id+"F17.imprint","IMPRINT",FACE,{"disambiguationData":[TD([[makeQuery(id+"F17.imprint","IMPRINT",EDGE,{"derivedFrom":sQuery(id+"F17.wireOp",EDGE,"E148")}),-1.0]])]});
            var Q2;
            Q2=makeQuery(id+"F17.imprint","IMPRINT",FACE,{"disambiguationData":[TD([[makeQuery(id+"F17.imprint","IMPRINT",EDGE,{"derivedFrom":sQuery(id+"F17.wireOp",EDGE,"E147")}),-1.0]])]});
            var Q3;
            {var subQ0=sQuery(id+"F17.wireOp",EDGE,"E170");var subQ1=sQuery(id+"F17.wireOp",EDGE,"E145");var subQ2=makeQuery(id+"F17.imprint","INTERSECT",VERTEX,{"disambiguationData":[OD(0.0)],"derivedFrom":[subQ1,subQ0]});Q3=makeQuery(id+"F17.imprint","IMPRINT",FACE,{"disambiguationData":[TD([[makeQuery(id+"F17.imprint","IMPRINT",EDGE,{"disambiguationData":[TD([[subQ2,-1.0]])],"derivedFrom":subQ1}),1.0]])]});}
            var Q4;
            {var subQ0=sQuery(id+"F17.wireOp",EDGE,"E170");var subQ1=sQuery(id+"F17.wireOp",EDGE,"E145");var subQ2=makeQuery(id+"F17.imprint","INTERSECT",VERTEX,{"disambiguationData":[OD(0.0)],"derivedFrom":[subQ1,subQ0]});Q4=makeQuery(id+"F17.imprint","IMPRINT",FACE,{"disambiguationData":[TD([[makeQuery(id+"F17.imprint","IMPRINT",EDGE,{"disambiguationData":[TD([[subQ2,-1.0]])],"derivedFrom":subQ1}),-1.0]])]});}
            var Q5;
            Q5=makeQuery(id+"F17.imprint","IMPRINT",FACE,{"disambiguationData":[TD([[makeQuery(id+"F17.imprint","IMPRINT",EDGE,{"derivedFrom":sQuery(id+"F17.wireOp",EDGE,"E148")}),1.0]])]});
            var Q6;
            Q6=makeQuery(id+"F17.imprint","IMPRINT",FACE,{"disambiguationData":[TD([[makeQuery(id+"F17.imprint","IMPRINT",EDGE,{"derivedFrom":sQuery(id+"F17.wireOp",EDGE,"E146")}),1.0]])]});
            var Q7;
            {var subQ0=sQuery(id+"F17.wireOp",EDGE,"E149");var subQ1=sQuery(id+"F17.wireOp",EDGE,"E145");var subQ2=makeQuery(id+"F17.imprint","INTERSECT",VERTEX,{"disambiguationData":[OD(0.0)],"derivedFrom":[subQ1,subQ0]});Q7=makeQuery(id+"F17.imprint","IMPRINT",FACE,{"disambiguationData":[TD([[makeQuery(id+"F17.imprint","IMPRINT",EDGE,{"disambiguationData":[TD([[subQ2,-1.0]])],"derivedFrom":subQ1}),1.0]])]});}
            var Q8;
            {var subQ0=sQuery(id+"F17.wireOp",EDGE,"E149");var subQ1=sQuery(id+"F17.wireOp",EDGE,"E145");var subQ2=makeQuery(id+"F17.imprint","INTERSECT",VERTEX,{"disambiguationData":[OD(0.0)],"derivedFrom":[subQ1,subQ0]});Q8=makeQuery(id+"F17.imprint","IMPRINT",FACE,{"disambiguationData":[TD([[makeQuery(id+"F17.imprint","IMPRINT",EDGE,{"disambiguationData":[TD([[subQ2,-1.0]])],"derivedFrom":subQ1}),-1.0]])]});}
            var Q9;
            Q9=makeQuery(id+"F17.imprint","IMPRINT",FACE,{"disambiguationData":[TD([[makeQuery(id+"F17.imprint","IMPRINT",EDGE,{"derivedFrom":sQuery(id+"F17.wireOp",EDGE,"E147")}),1.0]])]});
            var Q10;
            Q10=sQuery(id+"F17.wireOp",EDGE,"E168");
            var Q11;
            Q11=sQuery(id+"F17.wireOp",EDGE,"E170");
            var Q12;
            Q12=sQuery(id+"F17.wireOp",EDGE,"E167");
            var Q13;
            Q13=sQuery(id+"F17.wireOp",EDGE,"E169");
            var Q14;
            Q14=makeQuery(id+"F15.opLoft","SWEPT_FACE",FACE,{"disambiguationData":[OSD([sQuery(id+"F14.wireOp",EDGE,"E133"),sQuery(id+"F14.wireOp",EDGE,"E134"),sQuery(id+"F14.wireOp",EDGE,"E138"),sQuery(id+"F13.wireOp",EDGE,"E106"),sQuery(id+"F13.wireOp",EDGE,"E117.trimOffspring"),sQuery(id+"F13.wireOp",EDGE,"E124")])]});
            extrude(context, id + "F18", {"entities" : qUnion([Q0, Q1, Q2, Q3, Q4, Q5, Q6, Q7, Q8, Q9]), "operationType" : NewBodyOperationType.REMOVE, "surfaceEntities" : qUnion([Q10, Q11, Q12, Q13]), "oppositeDirection" : true, "depth" : 25 * mm, "endBoundEntityFace" : qUnion([Q14]), "offsetDistance" : 25 * mm});
        }
        {
            var Q0;
            Q0=makeQuery(id+"F10.imprint","IMPRINT",FACE,{"disambiguationData":[TD([[makeQuery(id+"F10.imprint","IMPRINT",EDGE,{"derivedFrom":sQuery(id+"F10.wireOp",EDGE,"E103")}),1.0]])]});
            extrude(context, id + "F19", {"entities" : qUnion([Q0]), "operationType" : NewBodyOperationType.REMOVE, "depth" : (3 - 1.4) * mm, "offsetDistance" : 25 * mm});
        }
        {
            var Q0;
            Q0=makeQuery(id+"F10.imprint","IMPRINT",FACE,{"disambiguationData":[TD([[makeQuery(id+"F10.imprint","IMPRINT",EDGE,{"derivedFrom":sQuery(id+"F10.wireOp",EDGE,"E104")}),1.0]])]});
            extrude(context, id + "F20", {"entities" : qUnion([Q0]), "operationType" : NewBodyOperationType.REMOVE, "depth" : 11 * mm, "offsetDistance" : 25 * mm});
        }
        {
            var Q0;
            Q0=makeQuery(id+"F10.imprint","IMPRINT",FACE,{"disambiguationData":[TD([[makeQuery(id+"F10.imprint","IMPRINT",EDGE,{"derivedFrom":sQuery(id+"F10.wireOp",EDGE,"E105")}),1.0]])]});
            extrude(context, id + "F21", {"entities" : qUnion([Q0]), "operationType" : NewBodyOperationType.REMOVE, "endBound" : BoundingType.THROUGH_ALL, "depth" : 25 * mm, "offsetDistance" : 25 * mm});
        }
    });
